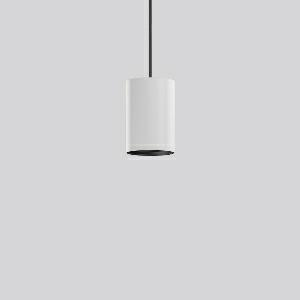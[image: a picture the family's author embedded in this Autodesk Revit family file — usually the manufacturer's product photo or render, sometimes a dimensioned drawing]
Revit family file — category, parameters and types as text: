
# Revit family: deecos_p_maxi_911535_002_76_51af
name_source: partatom
category: Lighting Fixtures
units: mm (PartAtom-declared; Revit-internal decimal feet)

## family parameters
Cut with Voids When Loaded = No
Host = Face
Light Source = No
Part Type = Normal
Room Calculation Point = No
Round Connector Dimension = Use Diameter
Shared = No

## types (1)
- DEECOS P maxi (1 x LED Modul 930, 2800 lm, 3000)
    Apparent Load = 25 VA
    Approval mark = CE
    CIE Flux Codes = 96 100 100 100 100
    Color Rendering = 90
    Color Temperature = 3000
    Default Elevation = 1800 mm
    Description = Series: DEECOS P maxi
Cylindrical pendant luminaire. Housing: die-cast aluminium, powder-coated. Canopy made of powder-coated sheet steel with magnetic attachment. Optical assembly with lens made of plastic (polycarbonate) for the best homogeneous light distribution - can be changed without tools. Best colour rendering index Ra>90. Transparent suspension cable 2 m, can be shortened. High quality converter without flickering and stroboscopic effect. The following accessories can be mounted without use of tools: interchangeable lenses, honeycomb louvre, clear and frosted diffusers, white interchangeable plastic ring. Decorative recessed suspension set available as accessory. 
Colour: traffic white, matt (RAL 9016)
Diameter: 123 mm
Height: 181 mm
Suspension length: 2000 mm
Lamp: LED
Socket: without socket
Colour temperature: 3000K
Colour rendering index (CRI): 92
System power: 25 W
Rated luminous flux: 2800 lm
Luminous efficiency: 112 lm/W
Control gear: Converter, dimmable, DALI
Protection class: I
Type of protection: IP 20
    Height = 181 mm
    Lamp = 1 x LED Modul 930
    Lamp Light Flux = 2800 lm
    Lamp count = 1
    Length = 123 mm
    Lifetime = 50000 h
    Luminous efficacy = 112 lm/W
    Manufacturer = RZB
    ModVariant = No
    Model = 911535.002.76
    Mounting Place = Ceiling
    Mounting Type = Pendant
    Number of Poles = 1
    OnlyDefault = Yes
    Power Factor = 1
    Product Name = DEECOS P maxi
    Product group = Pendant luminaires
    ProductGroupID = 902
    Protection Class = Protection class I
    Protection Degree = IP 20
    RLX_Detail_Level = 1
    RLX_Emergency_Light_Flux = 0 lm
    RLX_Emergency_Type = 0
    RLX_Emergency_Type_DB = No
    RlxData = <blob elided: 35605 chars, md5=6228004f>
    Socket = socket
    Standby Power = 0 W
    System Light Flux = 2800 lm
    System Power = 25 W
    Type Comments = Product without accessories
    Type Image = 911480.002.jpg
    URL = http://relux.com
    VarID = ---
    Voltage = 230 V
    Voltage Range = 220-240 V
    Weight = 0.00 kg
    Width = 0 mm  [stored 0 ft]

note: [stored X ft] marks values corroborated as IEEE doubles in the binary element streams (Revit-internal decimal feet)

## geometry (parser evidence)
native form markers: Blend x4, Sweep x9
no freeform markers — native parametric forms only
